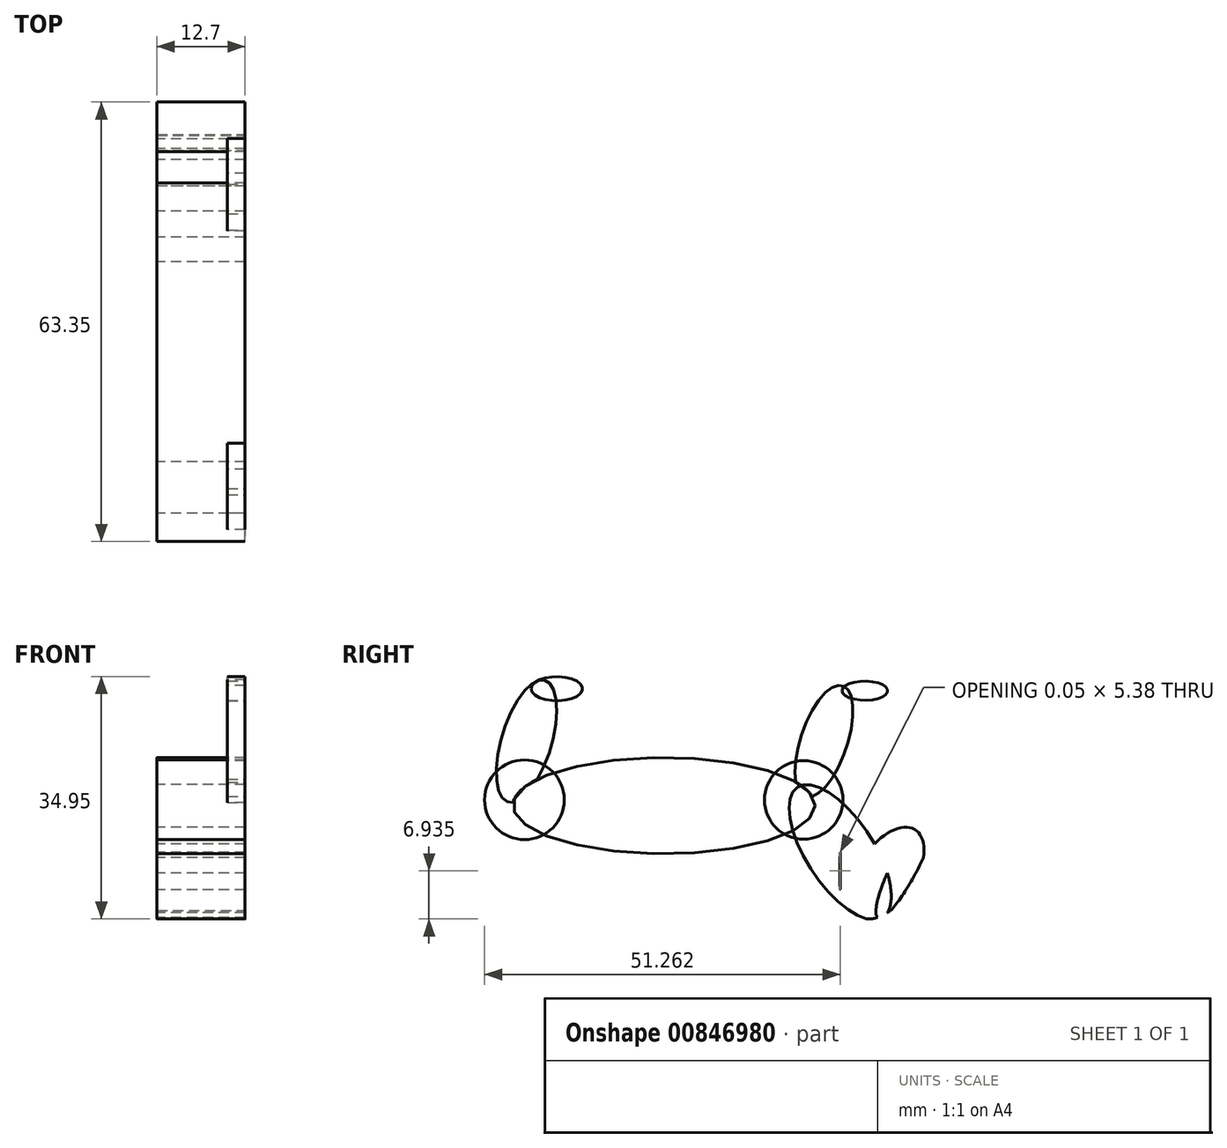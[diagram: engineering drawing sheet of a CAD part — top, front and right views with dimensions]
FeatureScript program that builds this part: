
annotation { "Feature Type Name" : "Feature", "Feature Type Description" : "" }
export const myFeature = defineFeature(function(context is Context, id is Id, definition is map)
    precondition{}
    {
        {
            var Q0;
            Q0=qCreatedBy(makeId("Right.planeOp"),FACE);
            var sketch = newSketch(context, id + "F0", { "sketchPlane" : qUnion([Q0])});
            skCircle(sketch, "E0", {"center": v(-20.11, -24.3) * mm, "radius": 5.74 * mm});
            skCircle(sketch, "E1", {"center": v(20.16, -24.32) * mm, "radius": 5.66 * mm});
            skSolve(sketch);
        }
        {
            var Q0;
            Q0=qCreatedBy(makeId("Right.planeOp"),FACE);
            var sketch = newSketch(context, id + "F1", { "sketchPlane" : qUnion([Q0])});
            skEllipse(sketch, "E2", {"center": v(0, -25.14) * mm, "majorRadius": 21.8 * mm, "minorRadius": 6.94 * mm, "majorAxis": v(1, 0)});
            skSolve(sketch);
        }
        {
            var Q0;
            Q0=makeQuery(id+"F0.imprint","IMPRINT",FACE,{"disambiguationData":[TD([[makeQuery(id+"F0.imprint","IMPRINT",EDGE,{"derivedFrom":sQuery(id+"F0.wireOp",EDGE,"E1")}),1.0]])]});
            var Q1;
            Q1=makeQuery(id+"F0.imprint","IMPRINT",FACE,{"disambiguationData":[TD([[makeQuery(id+"F0.imprint","IMPRINT",EDGE,{"derivedFrom":sQuery(id+"F0.wireOp",EDGE,"E0")}),1.0]])]});
            var Q2;
            Q2=makeQuery(id+"F1.imprint","IMPRINT",FACE,{"disambiguationData":[TD([[makeQuery(id+"F1.imprint","IMPRINT",EDGE,{"derivedFrom":sQuery(id+"F1.wireOp",EDGE,"E2")}),1.0]])]});
            extrude(context, id + "F2", {"entities" : qUnion([Q0, Q1, Q2]), "depth" : 12.7 * mm, "offsetDistance" : 25.4 * mm});
        }
        {
            var Q0;
            Q0=makeQuery(id+"F2.opExtrude","CAP_FACE",FACE,{"disambiguationData":[OSD([sQuery(id+"F1.wireOp",EDGE,"E2")])],"isStart":false});
            var sketch = newSketch(context, id + "F3", { "sketchPlane" : qUnion([Q0])});
            skEllipse(sketch, "E3", {"center": v(23.08, -15.86) * mm, "majorRadius": 8.45 * mm, "minorRadius": 3.36 * mm, "majorAxis": v(-0.32, -0.95)});
            skEllipse(sketch, "E4", {"center": v(-19.81, -15.86) * mm, "majorRadius": 9.17 * mm, "minorRadius": 3.61 * mm, "majorAxis": v(-0.29, -0.96)});
            skSolve(sketch);
        }
        {
            var Q0;
            {var subQ0=sQuery(id+"F3.wireOp",EDGE,"E3");var subQ1=makeQuery(id+"F2.opExtrude","CAP_EDGE",EDGE,{"disambiguationData":[OSD([sQuery(id+"F1.wireOp",EDGE,"E2")])],"isStart":false});var subQ2=makeQuery(id+"F3.imprint","INTERSECT",VERTEX,{"disambiguationData":[OD(0.0)],"derivedFrom":[subQ1,subQ0]});Q0=makeQuery(id+"F3.imprint","IMPRINT",FACE,{"disambiguationData":[TD([[makeQuery(id+"F3.imprint","IMPRINT",EDGE,{"disambiguationData":[TD([[subQ2,1.0]])],"derivedFrom":subQ0}),1.0]])]});}
            var Q1;
            {var subQ0=sQuery(id+"F3.wireOp",EDGE,"E4");var subQ1=makeQuery(id+"F2.opExtrude","CAP_EDGE",EDGE,{"disambiguationData":[OSD([sQuery(id+"F1.wireOp",EDGE,"E2")])],"isStart":false});var subQ2=makeQuery(id+"F3.imprint","INTERSECT",VERTEX,{"disambiguationData":[OD(0.0)],"derivedFrom":[subQ1,subQ0]});Q1=makeQuery(id+"F3.imprint","IMPRINT",FACE,{"disambiguationData":[TD([[makeQuery(id+"F3.imprint","IMPRINT",EDGE,{"disambiguationData":[TD([[subQ2,1.0]])],"derivedFrom":subQ0}),1.0]])]});}
            extrude(context, id + "F4", {"entities" : qUnion([Q0, Q1]), "oppositeDirection" : true, "depth" : 2.54 * mm, "offsetDistance" : 25.4 * mm});
        }
        {
            var Q0;
            Q0=makeQuery(id+"F4.opExtrude","CAP_FACE",FACE,{"disambiguationData":[OSD([sQuery(id+"F1.wireOp",EDGE,"E2"),sQuery(id+"F3.wireOp",EDGE,"E3")])],"isStart":true});
            var sketch = newSketch(context, id + "F5", { "sketchPlane" : qUnion([Q0])});
            skEllipse(sketch, "E5", {"center": v(28.97, -8.58) * mm, "majorRadius": 3.3 * mm, "minorRadius": 1.38 * mm, "majorAxis": v(-1, 0)});
            skEllipse(sketch, "E6", {"center": v(-15.43, -8.29) * mm, "majorRadius": 3.7 * mm, "minorRadius": 1.75 * mm, "majorAxis": v(-1, 0)});
            skSolve(sketch);
        }
        {
            var Q0;
            Q0 = qSketchRegion(id + "F5", true);
            var Q1;
            {var subQ0=sQuery(id+"F5.wireOp",EDGE,"E5");var subQ1=makeQuery(id+"F4.opExtrude","CAP_EDGE",EDGE,{"disambiguationData":[OSD([sQuery(id+"F3.wireOp",EDGE,"E3")])],"isStart":true});var subQ2=makeQuery(id+"F5.imprint","INTERSECT",VERTEX,{"disambiguationData":[OD(0.0)],"derivedFrom":[subQ1,subQ0]});Q1=makeQuery(id+"F5.imprint","IMPRINT",FACE,{"disambiguationData":[TD([[makeQuery(id+"F5.imprint","IMPRINT",EDGE,{"disambiguationData":[TD([[subQ2,1.0]])],"derivedFrom":subQ0}),1.0]])]});}
            extrude(context, id + "F6", {"entities" : qUnion([Q0, Q1]), "oppositeDirection" : true, "depth" : 2.54 * mm, "offsetDistance" : 25.4 * mm});
        }
        {
            var Q0;
            Q0=qCreatedBy(makeId("Right.planeOp"),FACE);
            var sketch = newSketch(context, id + "F7", { "sketchPlane" : qUnion([Q0])});
            skEllipse(sketch, "E7", {"center": v(25.41, -34.56) * mm, "majorRadius": 2.7 * mm, "minorRadius": 0.02 * mm, "majorAxis": v(0, 1)});
            skEllipse(sketch, "E8", {"center": v(25.41, -31.86) * mm, "majorRadius": 11.22 * mm, "minorRadius": 4.86 * mm, "majorAxis": v(-0.55, 0.84)});
            skEllipse(sketch, "E9", {"center": v(34.9, -33.55) * mm, "majorRadius": 8.76 * mm, "minorRadius": 1.86 * mm, "majorAxis": v(-0.46, -0.89)});
            skEllipse(sketch, "E10", {"center": v(32.21, -34.87) * mm, "majorRadius": 7.43 * mm, "minorRadius": 4.07 * mm, "majorAxis": v(-0.54, -0.84)});
            skPoint(sketch, "E10.perimeterSnap0", {"position": v(31.57, -41.25) * mm});
            skPoint(sketch, "E10.perimeterSnap1", {"position": v(30.89, -41.33) * mm});
            skSolve(sketch);
        }
        {
            var Q0;
            {var subQ0=sQuery(id+"F7.wireOp",EDGE,"E10");var subQ3=sQuery(id+"F7.wireOp",EDGE,"E8");var subQ4=makeQuery(id+"F7.imprint","INTERSECT",VERTEX,{"disambiguationData":[OD(3.0)],"derivedFrom":[subQ3,subQ0]});Q0=makeQuery(id+"F7.imprint","IMPRINT",FACE,{"disambiguationData":[TD([[makeQuery(id+"F7.imprint","IMPRINT",EDGE,{"disambiguationData":[TD([[subQ4,-1.0]])],"derivedFrom":subQ3}),-1.0]])]});}
            var Q1;
            {var subQ0=sQuery(id+"F7.wireOp",EDGE,"E10");var subQ1=sQuery(id+"F7.wireOp",EDGE,"E8");var subQ2=makeQuery(id+"F7.imprint","INTERSECT",VERTEX,{"disambiguationData":[OD(2.0)],"derivedFrom":[subQ1,subQ0]});Q1=makeQuery(id+"F7.imprint","IMPRINT",FACE,{"disambiguationData":[TD([[makeQuery(id+"F7.imprint","IMPRINT",EDGE,{"disambiguationData":[TD([[subQ2,1.0]])],"derivedFrom":subQ1}),-1.0]])]});}
            var Q2;
            {var subQ0=sQuery(id+"F7.wireOp",EDGE,"E10");var subQ1=sQuery(id+"F7.wireOp",EDGE,"E8");var subQ2=makeQuery(id+"F7.imprint","INTERSECT",VERTEX,{"disambiguationData":[OD(0.0)],"derivedFrom":[subQ1,subQ0]});Q2=makeQuery(id+"F7.imprint","IMPRINT",FACE,{"disambiguationData":[TD([[makeQuery(id+"F7.imprint","IMPRINT",EDGE,{"disambiguationData":[TD([[subQ2,1.0]])],"derivedFrom":subQ1}),1.0]])]});}
            var Q3;
            Q3=makeQuery(id+"F7.imprint","IMPRINT",FACE,{"disambiguationData":[TD([[makeQuery(id+"F7.imprint","IMPRINT",EDGE,{"derivedFrom":sQuery(id+"F7.wireOp",EDGE,"E7")}),-1.0]])]});
            extrude(context, id + "F8", {"entities" : qUnion([Q0, Q1, Q2, Q3]), "depth" : 12.7 * mm, "offsetDistance" : 25.4 * mm});
        }
    });
